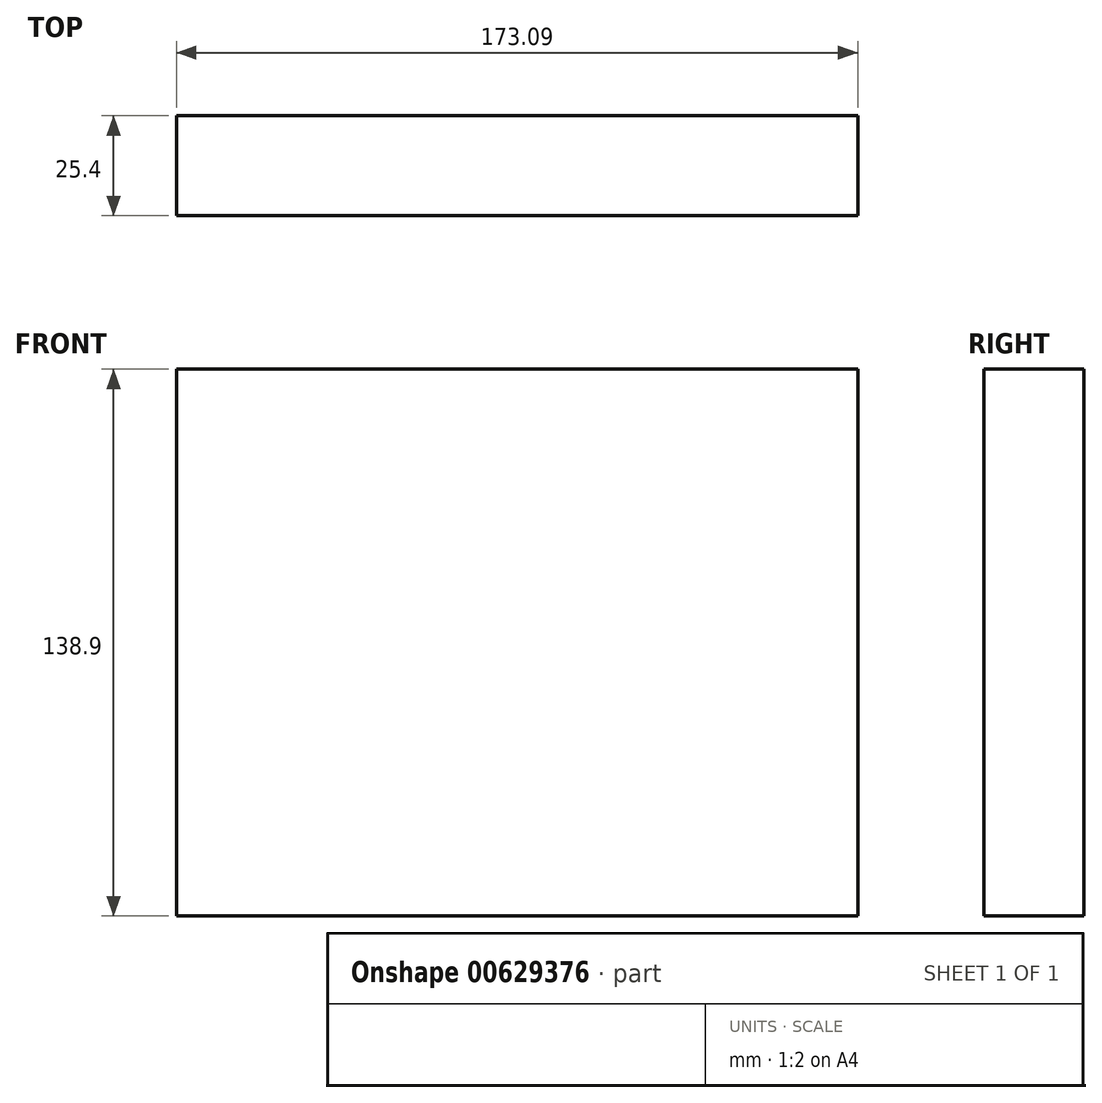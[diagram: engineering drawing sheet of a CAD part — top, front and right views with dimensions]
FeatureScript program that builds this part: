
annotation { "Feature Type Name" : "Feature", "Feature Type Description" : "" }
export const myFeature = defineFeature(function(context is Context, id is Id, definition is map)
    precondition{}
    {
        {
            var Q0;
            Q0=qCreatedBy(makeId("Front.planeOp"),FACE);
            var sketch = newSketch(context, id + "F0", { "sketchPlane" : qUnion([Q0])});
            skLineSegment(sketch, "E0.bottom", {"start": v(-91.37, 100.1) * mm, "end": v(81.72, 100.1) * mm});
            skLineSegment(sketch, "E0.top", {"start": v(-91.37, -38.79) * mm, "end": v(81.72, -38.79) * mm});
            skLineSegment(sketch, "E0.left", {"start": v(-91.37, 100.1) * mm, "end": v(-91.37, -38.79) * mm});
            skLineSegment(sketch, "E0.right", {"start": v(81.72, 100.1) * mm, "end": v(81.72, -38.79) * mm});
            skSolve(sketch);
        }
        {
            var Q0;
            Q0 = qSketchRegion(id + "F0", true);
            extrude(context, id + "F1", {"entities" : qUnion([Q0]), "depth" : 25.4 * mm, "offsetDistance" : 25.4 * mm});
        }
    });
